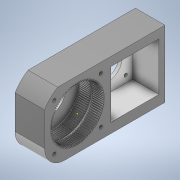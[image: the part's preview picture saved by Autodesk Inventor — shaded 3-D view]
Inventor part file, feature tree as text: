
AUTODESK INVENTOR PART (.ipt)
format: ipt  version: 2022 (Build 260153000, 153)  size: 1,581,568 bytes
history: mixed  units: mm
features: sketch x10, extrude x9, other x3, fillet x1, imported_body x1
ambient origin geometry x8: Origin, YZ Plane, XZ Plane, XY Plane, X Axis, Y Axis, Z Axis, Center Point
bodies: Solid1 (imported_parasolid)
feature tree (24):
  other  "Assembly2.iam"
  other  "96Gears_Stage_1_modified.ipt:1"
  other  "96Gears_Stage_2_modified.ipt:1"
  extrude  "Extrusion6"  TaperAngle=0.0deg  [1 undecoded]
  extrude  "Extrusion7"  Depth=25.0mm
  extrude  "Extrusion8"  Depth=24.0mm TaperAngle=0.0deg
  extrude  "Extrusion9"  Depth=25.0mm
  extrude  "Extrusion10"  Depth=5.5mm
  extrude  "Extrusion11"  Depth=5.2mm
  extrude  "Extrusion12"  Depth=4.0mm
  extrude  "Extrusion13"  Depth=10.0mm
  extrude  "Extrusion14"  Depth=3.0mm TaperAngle=0.0deg
  fillet  "Fillet1"  Radius=18.5mm
  sketch  "Sketch5"  dims[d0=10.0mm d20=0.0mm d21=0.0mm]
  sketch  "Sketch8"  dims[d22=25.0mm d23=0.0mm d24=50.0mm]
  sketch  "Sketch9"  dims[d25=10.0mm d26=0.0mm d32=24.0mm d33=0.0mm]
  sketch  "Sketch10"  dims[d37=3.0mm d38=25.0mm]
  sketch  "Sketch12"  dims[d39=0.0mm d40=0.0mm d41=5.5mm]
  sketch  "Sketch13"  dims[d42=5.2mm d43=5.2mm]
  sketch  "Sketch14"  dims[d44=0.0mm d45=0.0mm d46=4.0mm]
  sketch  "Sketch15"  dims[d47=10.0mm d48=0.0mm d49=25.5mm]
  sketch  "Sketch16"  dims[d50=3.0mm d51=0.0mm d52=3.0mm d53=0.0mm d54=18.5mm]
  sketch  "Sketch17"
  imported_body  NMx_Import_Brep_tag  [imported B-rep: ~803 faces, bbox_mm=[27.0, 61.027756, 110.0]]
note: 1 required parameter value undecoded (feature->parameter linkage not recoverable at this tier; creation-order binding heuristic only, values carry confidence <= 0.55)
